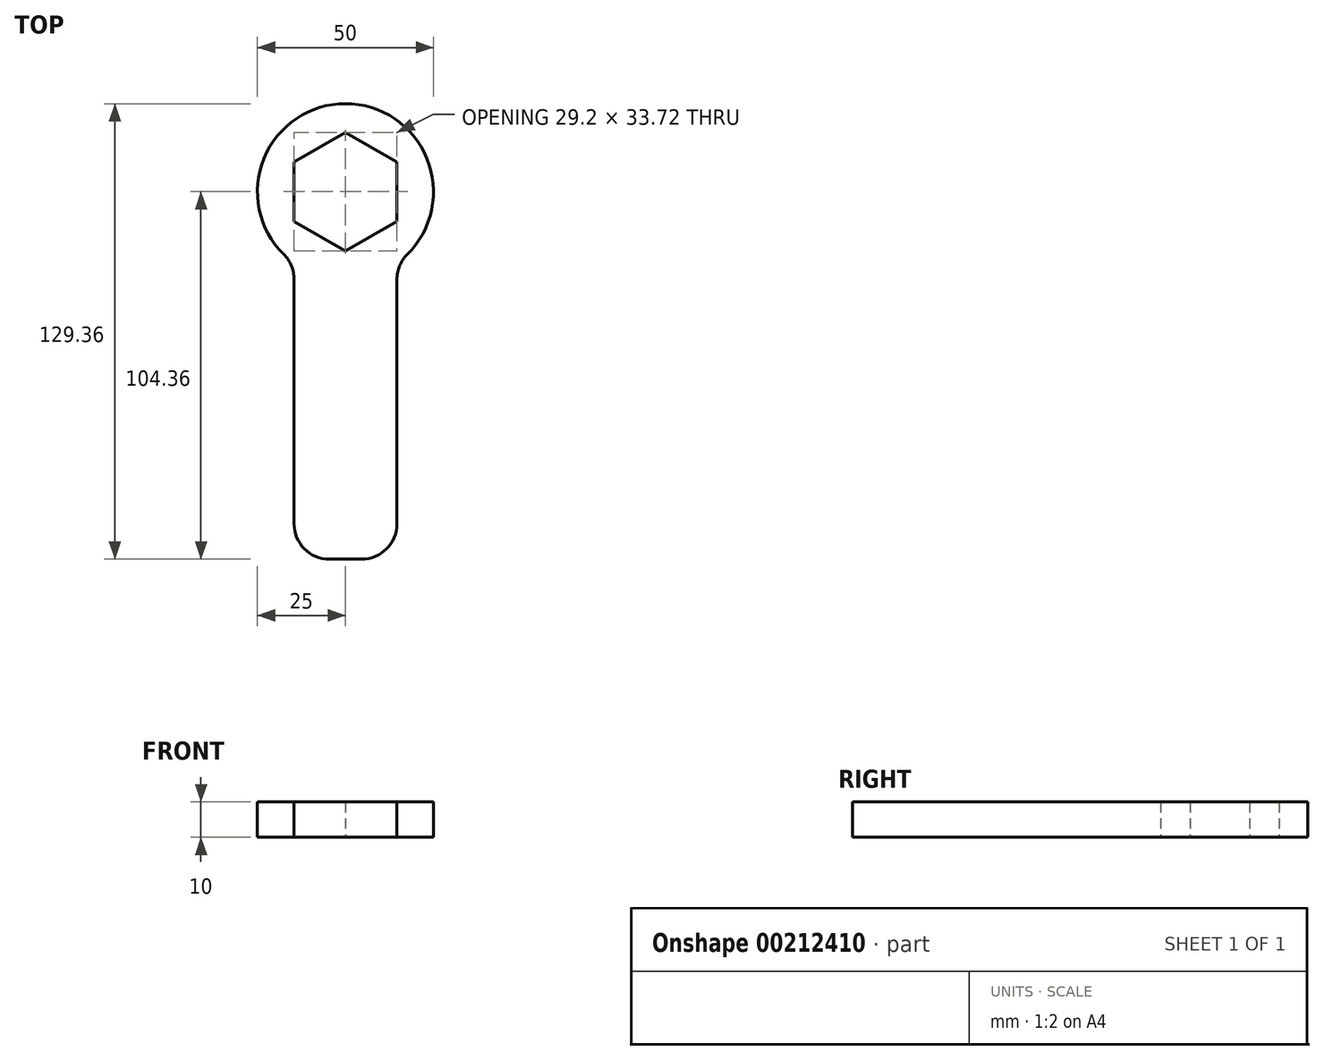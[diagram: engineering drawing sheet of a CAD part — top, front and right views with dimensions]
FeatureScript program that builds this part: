
annotation { "Feature Type Name" : "Feature", "Feature Type Description" : "" }
export const myFeature = defineFeature(function(context is Context, id is Id, definition is map)
    precondition{}
    {
        {
            var Q0;
            Q0=qCreatedBy(makeId("Top.planeOp"),FACE);
            var sketch = newSketch(context, id + "F0", { "sketchPlane" : qUnion([Q0])});
            skCircle(sketch, "E0", {"center": v(0, 0) * mm, "radius": 25 * mm});
            skCircle(sketch, "E1.cCircle", {"center": v(0, 0) * mm, "radius": 14.6 * mm, "construction": true});
            skLineSegment(sketch, "E1.0", {"start": v(14.6, 8.43) * mm, "end": v(14.6, -8.43) * mm});
            skLineSegment(sketch, "E1.1", {"start": v(14.6, -8.43) * mm, "end": v(0, -16.86) * mm});
            skLineSegment(sketch, "E1.2", {"start": v(0, -16.86) * mm, "end": v(-14.6, -8.43) * mm});
            skLineSegment(sketch, "E1.3", {"start": v(-14.6, -8.43) * mm, "end": v(-14.6, 8.43) * mm});
            skLineSegment(sketch, "E1.4", {"start": v(-14.6, 8.43) * mm, "end": v(0, 16.86) * mm});
            skLineSegment(sketch, "E1.5", {"start": v(0, 16.86) * mm, "end": v(14.6, 8.43) * mm});
            skPoint(sketch, "E1.0.midPoint", {"position": v(14.6, 0) * mm});
            skLineSegment(sketch, "E2", {"start": v(-14.6, -8.43) * mm, "end": v(-14.6, -104.36) * mm});
            skLineSegment(sketch, "E3", {"start": v(14.6, -8.43) * mm, "end": v(14.6, -104.36) * mm});
            skLineSegment(sketch, "E4", {"start": v(14.6, -104.36) * mm, "end": v(-14.6, -104.36) * mm});
            skSolve(sketch);
        }
        {
            var Q0;
            {var subQ4=sQuery(id+"F0.wireOp",EDGE,"E1.1");Q0=makeQuery(id+"F0.imprint","IMPRINT",FACE,{"disambiguationData":[TD([[makeQuery(id+"F0.imprint","IMPRINT",EDGE,{"derivedFrom":subQ4}),1.0]])]});}
            var Q1;
            {var subQ1=sQuery(id+"F0.wireOp",EDGE,"E1.0");Q1=makeQuery(id+"F0.imprint","IMPRINT",FACE,{"disambiguationData":[TD([[makeQuery(id+"F0.imprint","IMPRINT",EDGE,{"derivedFrom":subQ1}),1.0]])]});}
            var Q2;
            {var subQ5=sQuery(id+"F0.wireOp",EDGE,"E4");Q2=makeQuery(id+"F0.imprint","IMPRINT",FACE,{"disambiguationData":[TD([[makeQuery(id+"F0.imprint","IMPRINT",EDGE,{"derivedFrom":subQ5}),-1.0]])]});}
            extrude(context, id + "F1", {"entities" : qUnion([Q0, Q1, Q2]), "depth" : 10 * mm});
        }
        {
            var Q0;
            Q0=makeQuery(id+"F1.opExtrude","SWEPT_EDGE",EDGE,{"disambiguationData":[OSD([sQuery(id+"F0.wireOp",EDGE,"E0"),sQuery(id+"F0.wireOp",EDGE,"E3")])]});
            fillet(context, id + "F2", {"entities" : qUnion([Q0]), "radius" : 10 * mm, "tangentPropagation" : true, "allowEdgeOverflow" : false});
        }
        {
            var Q0;
            Q0=makeQuery(id+"F1.opExtrude","SWEPT_EDGE",EDGE,{"disambiguationData":[OSD([sQuery(id+"F0.wireOp",EDGE,"E0"),sQuery(id+"F0.wireOp",EDGE,"E2")])]});
            var Q1;
            Q1=makeQuery(id+"F1.opExtrude","SWEPT_EDGE",EDGE,{"disambiguationData":[OSD([sQuery(id+"F0.wireOp",EDGE,"E2"),sQuery(id+"F0.wireOp",EDGE,"E4")])]});
            var Q2;
            Q2=makeQuery(id+"F1.opExtrude","SWEPT_EDGE",EDGE,{"disambiguationData":[OSD([sQuery(id+"F0.wireOp",EDGE,"E3"),sQuery(id+"F0.wireOp",EDGE,"E4")])]});
            fillet(context, id + "F3", {"entities" : qUnion([Q0, Q1, Q2]), "radius" : 10 * mm, "tangentPropagation" : true, "allowEdgeOverflow" : false});
        }
    });
